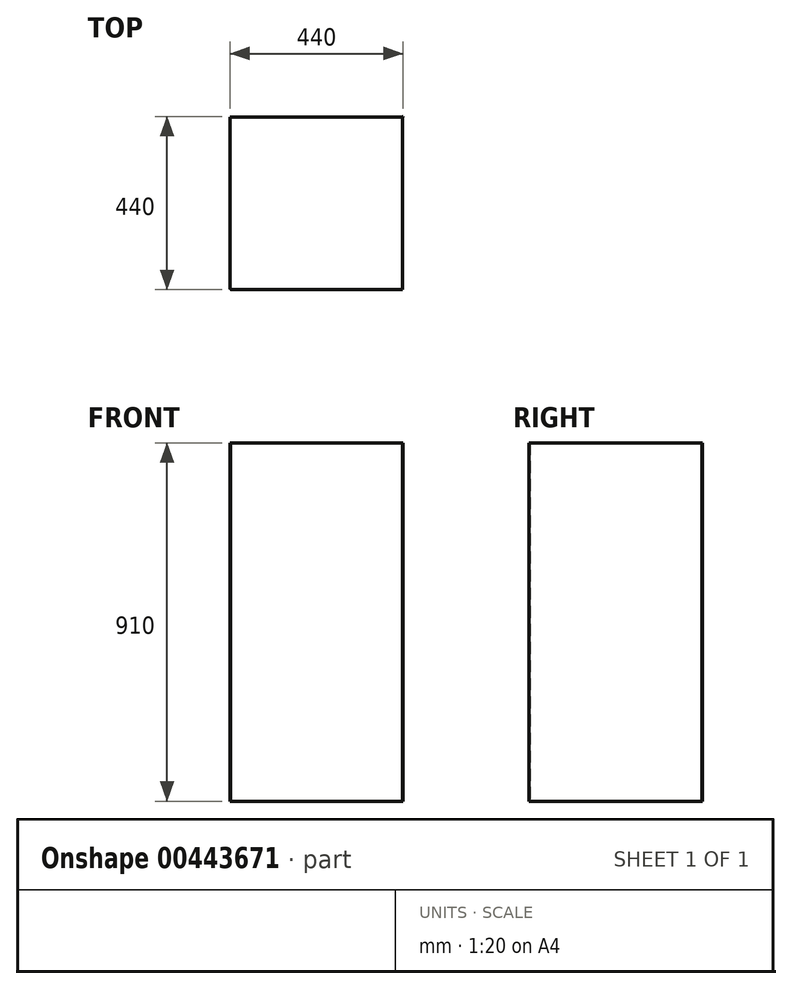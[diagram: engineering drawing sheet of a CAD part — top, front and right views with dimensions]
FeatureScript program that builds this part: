
annotation { "Feature Type Name" : "Feature", "Feature Type Description" : "" }
export const myFeature = defineFeature(function(context is Context, id is Id, definition is map)
    precondition{}
    {
        {
            var Q0;
            Q0=qCreatedBy(makeId("Top.planeOp"),FACE);
            var sketch = newSketch(context, id + "F0", { "sketchPlane" : qUnion([Q0])});
            skLineSegment(sketch, "E0", {"start": v(-199.98, -53.27) * mm, "end": v(240.02, -53.27) * mm});
            skLineSegment(sketch, "E1.top", {"start": v(-199.98, 386.73) * mm, "end": v(240.02, 386.73) * mm});
            skLineSegment(sketch, "E1.left", {"start": v(-199.98, -53.27) * mm, "end": v(-199.98, 386.73) * mm});
            skLineSegment(sketch, "E1.right", {"start": v(240.02, -53.27) * mm, "end": v(240.02, 386.73) * mm});
            skLineSegment(sketch, "E2", {"start": v(-199.98, -53.27) * mm, "end": v(-198.48, -53.27) * mm});
            skLineSegment(sketch, "E3", {"start": v(-199.98, -53.27) * mm, "end": v(-199.98, -51.77) * mm});
            skLineSegment(sketch, "E4", {"start": v(240.02, 386.73) * mm, "end": v(240.02, 385.23) * mm});
            skLineSegment(sketch, "E5", {"start": v(240.02, 386.73) * mm, "end": v(238.52, 386.73) * mm});
            skLineSegment(sketch, "E6", {"start": v(238.52, 386.73) * mm, "end": v(238.52, -53.27) * mm});
            skLineSegment(sketch, "E7", {"start": v(240.02, 385.23) * mm, "end": v(-199.98, 385.23) * mm});
            skLineSegment(sketch, "E8", {"start": v(-199.98, -51.77) * mm, "end": v(238.52, -51.77) * mm});
            skLineSegment(sketch, "E9", {"start": v(-198.48, -53.27) * mm, "end": v(-198.48, 385.23) * mm});
            skSolve(sketch);
        }
        {
            var Q0;
            {var subQ0=sQuery(id+"F0.wireOp",EDGE,"E2");Q0=makeQuery(id+"F0.imprint","IMPRINT",FACE,{"disambiguationData":[TD([[makeQuery(id+"F0.imprint","IMPRINT",EDGE,{"derivedFrom":subQ0}),1.0]])]});}
            var Q1;
            {var subQ0=sQuery(id+"F0.wireOp",EDGE,"E4");Q1=makeQuery(id+"F0.imprint","IMPRINT",FACE,{"disambiguationData":[TD([[makeQuery(id+"F0.imprint","IMPRINT",EDGE,{"derivedFrom":subQ0}),-1.0]])]});}
            var Q2;
            {var subQ4=sQuery(id+"F0.wireOp",EDGE,"E1.right");Q2=makeQuery(id+"F0.imprint","IMPRINT",FACE,{"disambiguationData":[TD([[makeQuery(id+"F0.imprint","IMPRINT",EDGE,{"derivedFrom":subQ4}),1.0]])]});}
            var Q3;
            {var subQ1=sQuery(id+"F0.wireOp",EDGE,"E1.top");Q3=makeQuery(id+"F0.imprint","IMPRINT",FACE,{"disambiguationData":[TD([[makeQuery(id+"F0.imprint","IMPRINT",EDGE,{"derivedFrom":subQ1}),-1.0]])]});}
            var Q4;
            {var subQ1=sQuery(id+"F0.wireOp",EDGE,"E1.left");var subQ3=sQuery(id+"F0.wireOp",EDGE,"E7");var subQ4=makeQuery(id+"F0.imprint","INTERSECT",VERTEX,{"derivedFrom":[subQ1,subQ3]});Q4=makeQuery(id+"F0.imprint","IMPRINT",FACE,{"disambiguationData":[TD([[makeQuery(id+"F0.imprint","IMPRINT",EDGE,{"disambiguationData":[TD([[subQ4,1.0]])],"derivedFrom":subQ3}),1.0]])]});}
            var Q5;
            {var subQ1=sQuery(id+"F0.wireOp",EDGE,"E0");var subQ3=sQuery(id+"F0.wireOp",EDGE,"E6");var subQ4=makeQuery(id+"F0.imprint","INTERSECT",VERTEX,{"derivedFrom":[subQ1,subQ3]});Q5=makeQuery(id+"F0.imprint","IMPRINT",FACE,{"disambiguationData":[TD([[makeQuery(id+"F0.imprint","IMPRINT",EDGE,{"disambiguationData":[TD([[subQ4,1.0]])],"derivedFrom":subQ3}),-1.0]])]});}
            extrude(context, id + "F1", {"entities" : qUnion([Q0, Q1, Q2, Q3, Q4, Q5]), "depth" : 910 * mm});
        }
        {
            var Q0;
            Q0=makeQuery(id+"F1.opExtrude","CAP_FACE",FACE,{"disambiguationData":[OSD([sQuery(id+"F0.wireOp",EDGE,"E0"),sQuery(id+"F0.wireOp",EDGE,"E1.top"),sQuery(id+"F0.wireOp",EDGE,"E1.left"),sQuery(id+"F0.wireOp",EDGE,"E1.right"),sQuery(id+"F0.wireOp",EDGE,"E2"),sQuery(id+"F0.wireOp",EDGE,"E3"),sQuery(id+"F0.wireOp",EDGE,"E4"),sQuery(id+"F0.wireOp",EDGE,"E5"),sQuery(id+"F0.wireOp",EDGE,"E6"),sQuery(id+"F0.wireOp",EDGE,"E7"),sQuery(id+"F0.wireOp",EDGE,"E8"),sQuery(id+"F0.wireOp",EDGE,"E9")])],"isStart":false});
            var sketch = newSketch(context, id + "F2", { "sketchPlane" : qUnion([Q0])});
            skLineSegment(sketch, "E10.bottom", {"start": v(238.52, -51.77) * mm, "end": v(-198.48, -51.77) * mm});
            skLineSegment(sketch, "E10.top", {"start": v(238.52, 385.23) * mm, "end": v(-198.48, 385.23) * mm});
            skLineSegment(sketch, "E10.left", {"start": v(238.52, -51.77) * mm, "end": v(238.52, 385.23) * mm});
            skLineSegment(sketch, "E10.right", {"start": v(-198.48, -51.77) * mm, "end": v(-198.48, 385.23) * mm});
            skSolve(sketch);
        }
        {
            var Q0;
            Q0 = qSketchRegion(id + "F2", true);
            extrude(context, id + "F3", {"entities" : qUnion([Q0]), "operationType" : NewBodyOperationType.ADD, "oppositeDirection" : true, "depth" : 1.5 * mm});
        }
    });
